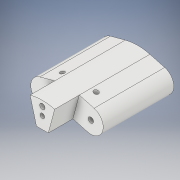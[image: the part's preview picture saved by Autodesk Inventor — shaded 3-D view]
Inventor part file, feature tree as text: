
AUTODESK INVENTOR PART (.ipt)
format: ipt  version: 2017 SP1 (Build 210196100, 196)  size: 160,256 bytes
history: native  units: in
note: dims shown in document units (in); Inventor stores cm internally (conversion verified against a paired STEP export)
features: extrude x5, sketch x5
ambient origin geometry x8: Origin, YZ Plane, XZ Plane, XY Plane, X Axis, Y Axis, Z Axis, Center Point
bodies: Solid1 (feature_tree)
feature tree (10):
  extrude  "Extrusion1"  Depth=1.811in TaperAngle=0.0deg
  extrude  "Extrusion2"  Depth=0.1378in
  extrude  "Extrusion3"  Depth=0.5118in
  extrude  "Extrusion4"  Depth=0.6299in TaperAngle=0.0deg
  extrude  "Extrusion7"  Depth=0.6299in TaperAngle=0.0deg
  sketch  "Sketch1"  dims[d0=0.6299in d1=0.6299in d2=0.6299in d3=0.3937in d4=0.3937in d5=0.6299in d6=0.6299in d7=75.0deg d9=1.811in d10=0.0in]
  sketch  "Sketch2"  dims[d11=0.1378in d12=0.1378in]
  sketch  "Sketch3"  dims[d13=0.1378in d14=0.5118in]
  sketch  "Sketch4"  dims[d15=1.811in d16=0.0in d17=0.6299in d18=0.0in]
  sketch  "Sketch7"  dims[d19=0.1181in d20=0.6299in d21=0.0in d28=0.1181in d29=0.1181in d30=0.8661in d31=0.9449in d32=0.3937in d33=0.0in]
